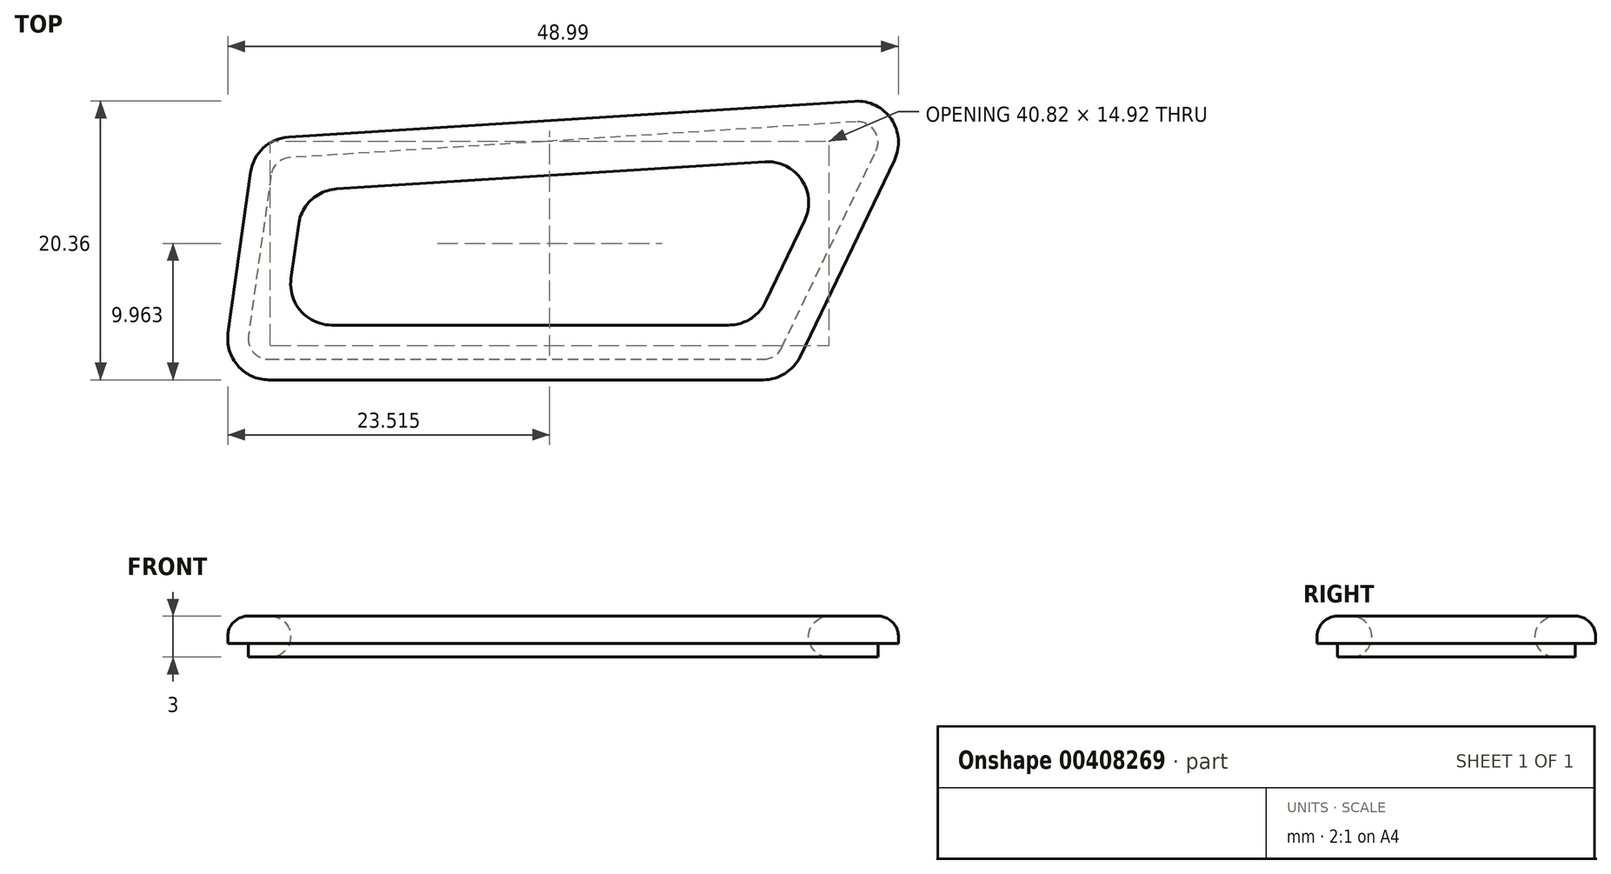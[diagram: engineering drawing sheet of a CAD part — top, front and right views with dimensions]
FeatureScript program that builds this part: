
annotation { "Feature Type Name" : "Feature", "Feature Type Description" : "" }
export const myFeature = defineFeature(function(context is Context, id is Id, definition is map)
    precondition{}
    {
        {
            var Q0;
            Q0=qCreatedBy(makeId("Top.planeOp"),FACE);
            var sketch = newSketch(context, id + "F0", { "sketchPlane" : qUnion([Q0])});
            skLineSegment(sketch, "E0", {"start": v(10.86, 3.76) * mm, "end": v(39.86, 3.76) * mm});
            skLineSegment(sketch, "E1", {"start": v(42.57, 5.46) * mm, "end": v(45.41, 11.4) * mm});
            skLineSegment(sketch, "E2", {"start": v(42.52, 15.69) * mm, "end": v(11.22, 13.7) * mm});
            skLineSegment(sketch, "E3", {"start": v(8.44, 11.13) * mm, "end": v(7.9, 7.18) * mm});
            skLineSegment(sketch, "E4.0", {"start": v(4.93, 14.91) * mm, "end": v(3.3, 3.18) * mm});
            skLineSegment(sketch, "E4.1", {"start": v(49.08, 20.11) * mm, "end": v(7.71, 17.5) * mm});
            skLineSegment(sketch, "E4.2", {"start": v(45.09, 1.46) * mm, "end": v(51.97, 15.82) * mm});
            skLineSegment(sketch, "E4.3", {"start": v(6.27, -0.24) * mm, "end": v(42.38, -0.24) * mm});
            skPoint(sketch, "E5.visualSharp", {"position": v(5.27, 17.34) * mm});
            skArc(sketch, "E5.filletArc", {"start": v(7.71, 17.5) * mm, "mid": v(5.86, 16.7) * mm, "end": v(4.93, 14.91) * mm});
            skPoint(sketch, "E6.visualSharp", {"position": v(54.18, 20.43) * mm});
            skArc(sketch, "E6.filletArc", {"start": v(51.97, 15.82) * mm, "mid": v(51.75, 18.8) * mm, "end": v(49.08, 20.11) * mm});
            skPoint(sketch, "E7.visualSharp", {"position": v(44.27, -0.24) * mm});
            skArc(sketch, "E7.filletArc", {"start": v(42.38, -0.24) * mm, "mid": v(43.98, 0.22) * mm, "end": v(45.09, 1.46) * mm});
            skPoint(sketch, "E8.visualSharp", {"position": v(2.82, -0.24) * mm});
            skArc(sketch, "E8.filletArc", {"start": v(3.3, 3.18) * mm, "mid": v(4, 0.8) * mm, "end": v(6.27, -0.24) * mm});
            skPoint(sketch, "E9.visualSharp", {"position": v(8.78, 13.55) * mm});
            skArc(sketch, "E9.filletArc", {"start": v(11.22, 13.7) * mm, "mid": v(9.37, 12.91) * mm, "end": v(8.44, 11.13) * mm});
            skPoint(sketch, "E10.visualSharp", {"position": v(47.63, 16.01) * mm});
            skArc(sketch, "E10.filletArc", {"start": v(45.41, 11.4) * mm, "mid": v(45.2, 14.37) * mm, "end": v(42.52, 15.69) * mm});
            skPoint(sketch, "E11.visualSharp", {"position": v(41.75, 3.76) * mm});
            skArc(sketch, "E11.filletArc", {"start": v(39.86, 3.76) * mm, "mid": v(41.46, 4.22) * mm, "end": v(42.57, 5.46) * mm});
            skPoint(sketch, "E12.visualSharp", {"position": v(7.41, 3.76) * mm});
            skArc(sketch, "E12.filletArc", {"start": v(7.9, 7.18) * mm, "mid": v(8.6, 4.8) * mm, "end": v(10.86, 3.76) * mm});
            skSolve(sketch);
        }
        {
            var Q0;
            Q0=makeQuery(id+"F0.imprint","IMPRINT",FACE,{"disambiguationData":[TD([[makeQuery(id+"F0.imprint","IMPRINT",EDGE,{"derivedFrom":sQuery(id+"F0.wireOp",EDGE,"E0")}),-1.0]])]});
            extrude(context, id + "F1", {"entities" : qUnion([Q0]), "oppositeDirection" : true, "depth" : 3 * mm});
        }
        {
            var Q0;
            Q0=makeQuery(id+"F1.opExtrude","CAP_EDGE",EDGE,{"disambiguationData":[OSD([sQuery(id+"F0.wireOp",EDGE,"E4.3")])],"isStart":true});
            var Q1;
            Q1=makeQuery(id+"F1.opExtrude","CAP_EDGE",EDGE,{"disambiguationData":[OSD([sQuery(id+"F0.wireOp",EDGE,"E4.2")])],"isStart":true});
            var Q2;
            Q2=makeQuery(id+"F1.opExtrude","CAP_EDGE",EDGE,{"disambiguationData":[OSD([sQuery(id+"F0.wireOp",EDGE,"E4.1")])],"isStart":true});
            var Q3;
            Q3=makeQuery(id+"F1.opExtrude","CAP_EDGE",EDGE,{"disambiguationData":[OSD([sQuery(id+"F0.wireOp",EDGE,"E4.0")])],"isStart":true});
            var Q4;
            Q4=makeQuery(id+"F1.opExtrude","CAP_EDGE",EDGE,{"disambiguationData":[OSD([sQuery(id+"F0.wireOp",EDGE,"E0")])],"isStart":true});
            var Q5;
            Q5=makeQuery(id+"F1.opExtrude","CAP_EDGE",EDGE,{"disambiguationData":[OSD([sQuery(id+"F0.wireOp",EDGE,"E3")])],"isStart":true});
            var Q6;
            Q6=makeQuery(id+"F1.opExtrude","CAP_EDGE",EDGE,{"disambiguationData":[OSD([sQuery(id+"F0.wireOp",EDGE,"E1")])],"isStart":true});
            var Q7;
            Q7=makeQuery(id+"F1.opExtrude","CAP_EDGE",EDGE,{"disambiguationData":[OSD([sQuery(id+"F0.wireOp",EDGE,"E2")])],"isStart":true});
            var Q8;
            Q8=makeQuery(id+"F1.opExtrude","CAP_EDGE",EDGE,{"disambiguationData":[OSD([sQuery(id+"F0.wireOp",EDGE,"E3")])],"isStart":false});
            var Q9;
            Q9=makeQuery(id+"F1.opExtrude","CAP_EDGE",EDGE,{"disambiguationData":[OSD([sQuery(id+"F0.wireOp",EDGE,"E0")])],"isStart":false});
            var Q10;
            Q10=makeQuery(id+"F1.opExtrude","CAP_EDGE",EDGE,{"disambiguationData":[OSD([sQuery(id+"F0.wireOp",EDGE,"E2")])],"isStart":false});
            var Q11;
            Q11=makeQuery(id+"F1.opExtrude","CAP_EDGE",EDGE,{"disambiguationData":[OSD([sQuery(id+"F0.wireOp",EDGE,"E1")])],"isStart":false});
            fillet(context, id + "F2", {"entities" : qUnion([Q0, Q1, Q2, Q3, Q4, Q5, Q6, Q7, Q8, Q9, Q10, Q11]), "radius" : 1.5 * mm, "tangentPropagation" : true, "allowEdgeOverflow" : false});
        }
        {
            var Q0;
            Q0=makeQuery(id+"F1.opExtrude","CAP_FACE",FACE,{"disambiguationData":[OSD([sQuery(id+"F0.wireOp",EDGE,"E0"),sQuery(id+"F0.wireOp",EDGE,"E1"),sQuery(id+"F0.wireOp",EDGE,"E2"),sQuery(id+"F0.wireOp",EDGE,"E3"),sQuery(id+"F0.wireOp",EDGE,"E4.0"),sQuery(id+"F0.wireOp",EDGE,"E4.1"),sQuery(id+"F0.wireOp",EDGE,"E4.2"),sQuery(id+"F0.wireOp",EDGE,"E4.3")])],"isStart":false});
            cPlane(context, id + "F3", {"entities" : qUnion([Q0]), "cplaneType" : CPlaneType.OFFSET, "offset" : 0 * mm, "width" : 150 * mm, "height" : 150 * mm});
        }
        {
            var Q0;
            Q0=qCreatedBy(id+"F3.planeOp",FACE);
            var sketch = newSketch(context, id + "F4", { "sketchPlane" : qUnion([Q0])});
            skLineSegment(sketch, "E13.0", {"start": v(4.93, -14.91) * mm, "end": v(4.93, -14.91) * mm});
            skLineSegment(sketch, "E14.0", {"start": v(4.93, -14.91) * mm, "end": v(3.3, -3.18) * mm});
            skPoint(sketch, "E15.0", {"position": v(0, 0) * mm});
            skArc(sketch, "E16.0", {"start": v(3.3, -3.18) * mm, "mid": v(4, -0.8) * mm, "end": v(6.27, 0.24) * mm});
            skLineSegment(sketch, "E17.0", {"start": v(6.27, 0.24) * mm, "end": v(42.38, 0.24) * mm});
            skArc(sketch, "E18.0", {"start": v(42.38, 0.24) * mm, "mid": v(43.98, -0.22) * mm, "end": v(45.09, -1.46) * mm});
            skLineSegment(sketch, "E19.0", {"start": v(45.09, -1.46) * mm, "end": v(51.97, -15.82) * mm});
            skLineSegment(sketch, "E20.0", {"start": v(49.08, -20.11) * mm, "end": v(7.71, -17.5) * mm});
            skArc(sketch, "E21.0", {"start": v(51.97, -15.82) * mm, "mid": v(51.75, -18.8) * mm, "end": v(49.08, -20.11) * mm});
            skArc(sketch, "E22.0", {"start": v(7.71, -17.5) * mm, "mid": v(5.86, -16.7) * mm, "end": v(4.93, -14.91) * mm});
            skLineSegment(sketch, "E23.0", {"start": v(49.17, -18.61) * mm, "end": v(7.8, -16) * mm});
            skArc(sketch, "E23.1", {"start": v(50.62, -16.47) * mm, "mid": v(50.5, -17.96) * mm, "end": v(49.17, -18.61) * mm});
            skArc(sketch, "E23.2", {"start": v(7.8, -16) * mm, "mid": v(6.88, -15.6) * mm, "end": v(6.42, -14.7) * mm});
            skLineSegment(sketch, "E23.3", {"start": v(43.73, -2.11) * mm, "end": v(50.62, -16.47) * mm});
            skLineSegment(sketch, "E23.4", {"start": v(6.42, -14.7) * mm, "end": v(4.78, -2.97) * mm});
            skArc(sketch, "E23.5", {"start": v(4.78, -2.97) * mm, "mid": v(5.13, -1.78) * mm, "end": v(6.27, -1.26) * mm});
            skLineSegment(sketch, "E23.6", {"start": v(6.27, -1.26) * mm, "end": v(42.38, -1.26) * mm});
            skArc(sketch, "E23.7", {"start": v(42.38, -1.26) * mm, "mid": v(43.18, -1.5) * mm, "end": v(43.73, -2.11) * mm});
            skSolve(sketch);
        }
        {
            var Q0;
            Q0=makeQuery(id+"F4.imprint","IMPRINT",FACE,{"disambiguationData":[TD([[makeQuery(id+"F4.imprint","IMPRINT",EDGE,{"derivedFrom":sQuery(id+"F4.wireOp",EDGE,"E13.0")}),-1.0]])]});
            var Q1;
            Q1=makeQuery(id+"F4.imprint","IMPRINT",FACE,{"disambiguationData":[TD([[makeQuery(id+"F4.imprint","IMPRINT",EDGE,{"derivedFrom":sQuery(id+"F4.wireOp",EDGE,"E14.0")}),-1.0]])]});
            extrude(context, id + "F5", {"entities" : qUnion([Q0, Q1]), "operationType" : NewBodyOperationType.REMOVE, "oppositeDirection" : true, "depth" : 1 * mm});
        }
    });
